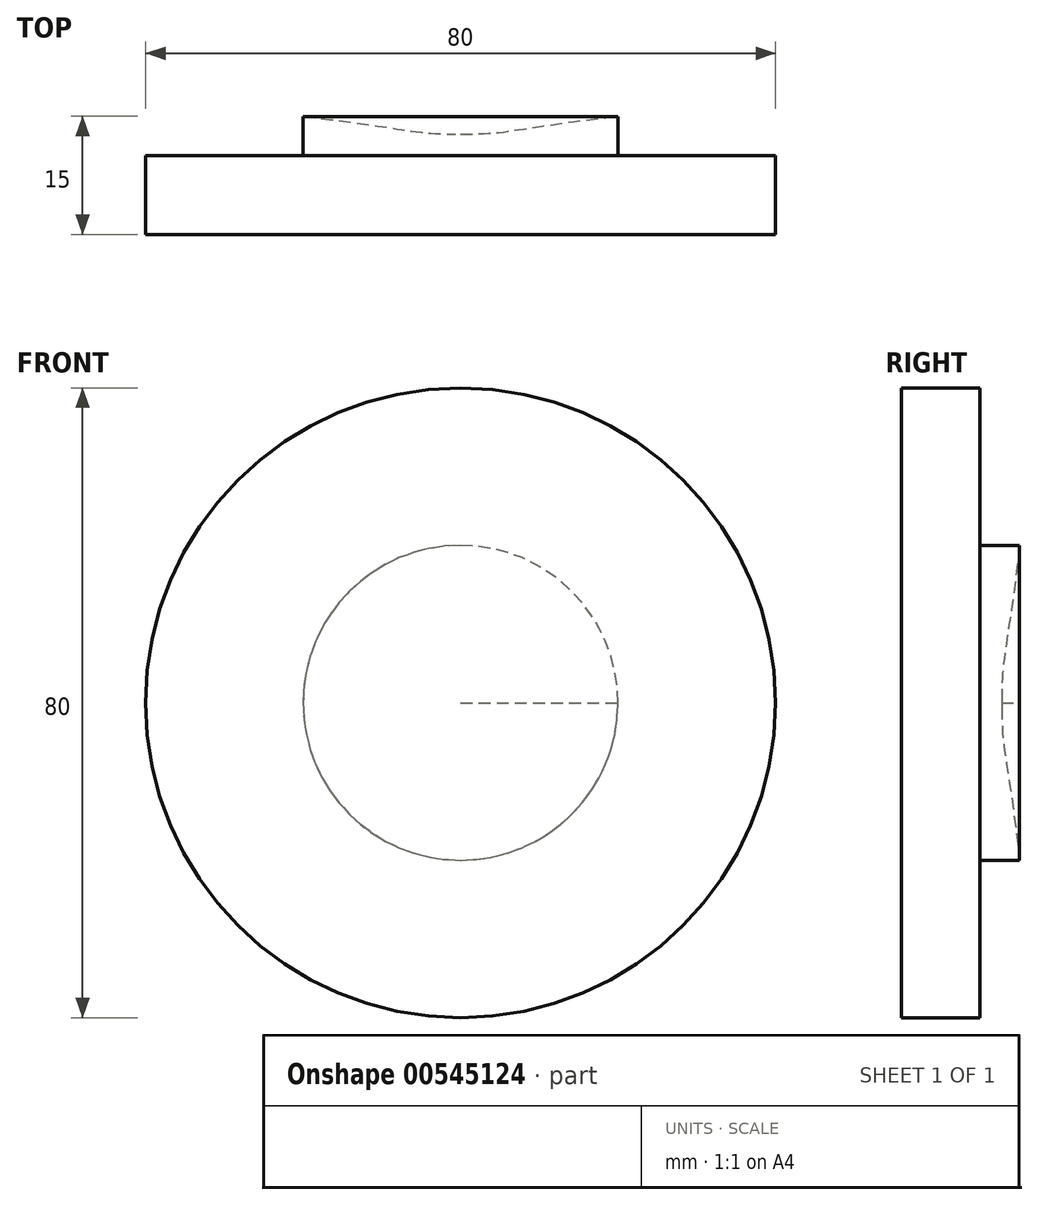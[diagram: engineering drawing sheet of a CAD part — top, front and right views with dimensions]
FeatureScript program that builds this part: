
annotation { "Feature Type Name" : "Feature", "Feature Type Description" : "" }
export const myFeature = defineFeature(function(context is Context, id is Id, definition is map)
    precondition{}
    {
        {
            var Q0;
            Q0=qCreatedBy(makeId("Top.planeOp"),FACE);
            var sketch = newSketch(context, id + "F0", { "sketchPlane" : qUnion([Q0])});
            skLineSegment(sketch, "E0", {"start": v(0, 17.13) * mm, "end": v(0, 4.38) * mm});
            skLineSegment(sketch, "E1", {"start": v(0, 4.38) * mm, "end": v(40, 4.38) * mm});
            skLineSegment(sketch, "E2", {"start": v(40, 4.38) * mm, "end": v(40, 14.38) * mm});
            skLineSegment(sketch, "E3", {"start": v(40, 14.38) * mm, "end": v(20, 14.38) * mm});
            skLineSegment(sketch, "E4", {"start": v(20, 14.38) * mm, "end": v(20, 19.38) * mm});
            skFitSpline(sketch, "E5", {"points": [v(0, 17.13) * mm, v(20, 19.38) * mm], "startDerivative": vector(19.27, -0.2) * mm, "endDerivative": vector(37.91, 4.08) * mm});
            skSolve(sketch);
        }
        {
            var Q0;
            Q0=makeQuery(id+"F0.imprint","IMPRINT",FACE,{"disambiguationData":[TD([[makeQuery(id+"F0.imprint","IMPRINT",EDGE,{"derivedFrom":sQuery(id+"F0.wireOp",EDGE,"E0")}),1.0]])]});
            var Q1;
            Q1=sQuery(id+"F0.wireOp",EDGE,"E0");
            revolve(context, id + "F1", {"entities" : qUnion([Q0]), "axis" : qUnion([Q1]), "revolveType" : RevolveType.FULL});
        }
    });
